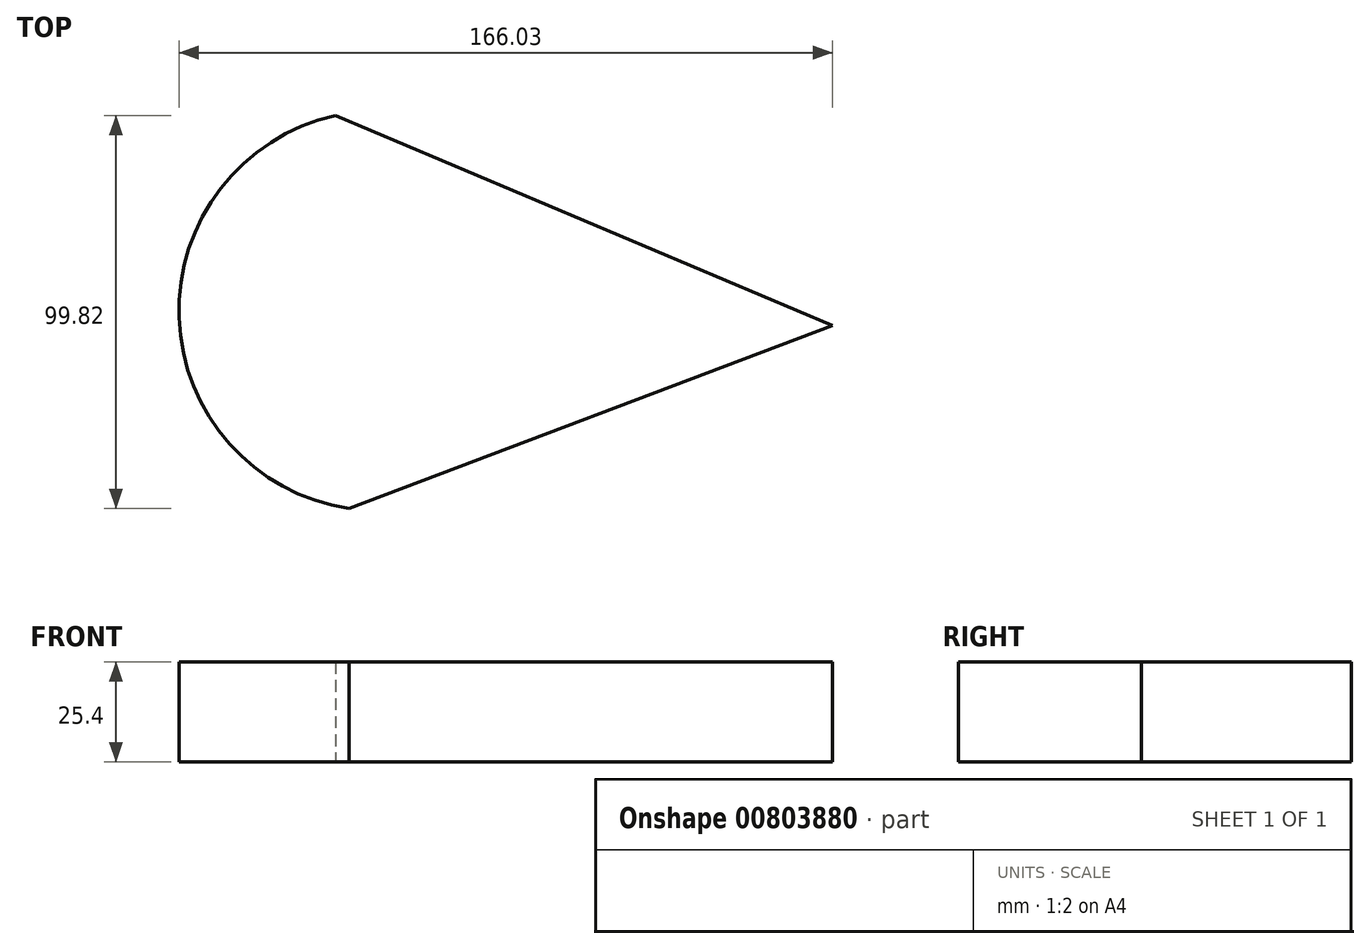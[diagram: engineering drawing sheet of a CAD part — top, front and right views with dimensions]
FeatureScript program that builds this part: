
annotation { "Feature Type Name" : "Feature", "Feature Type Description" : "" }
export const myFeature = defineFeature(function(context is Context, id is Id, definition is map)
    precondition{}
    {
        {
            var Q0;
            Q0=qCreatedBy(makeId("Top.planeOp"),FACE);
            var sketch = newSketch(context, id + "F0", { "sketchPlane" : qUnion([Q0])});
            skArc(sketch, "E0", {"start": v(-144, 53.35) * mm, "mid": v(-183.74, 2) * mm, "end": v(-140.53, -46.47) * mm});
            skLineSegment(sketch, "E1", {"start": v(-144, 53.35) * mm, "end": v(-17.74, 0) * mm});
            skLineSegment(sketch, "E2", {"start": v(-17.74, 0) * mm, "end": v(-140.53, -46.47) * mm});
            skSolve(sketch);
        }
        {
            var Q0;
            Q0 = qSketchRegion(id + "F0", true);
            extrude(context, id + "F1", {"entities" : qUnion([Q0]), "depth" : 25.4 * mm, "offsetDistance" : 25.4 * mm});
        }
    });
